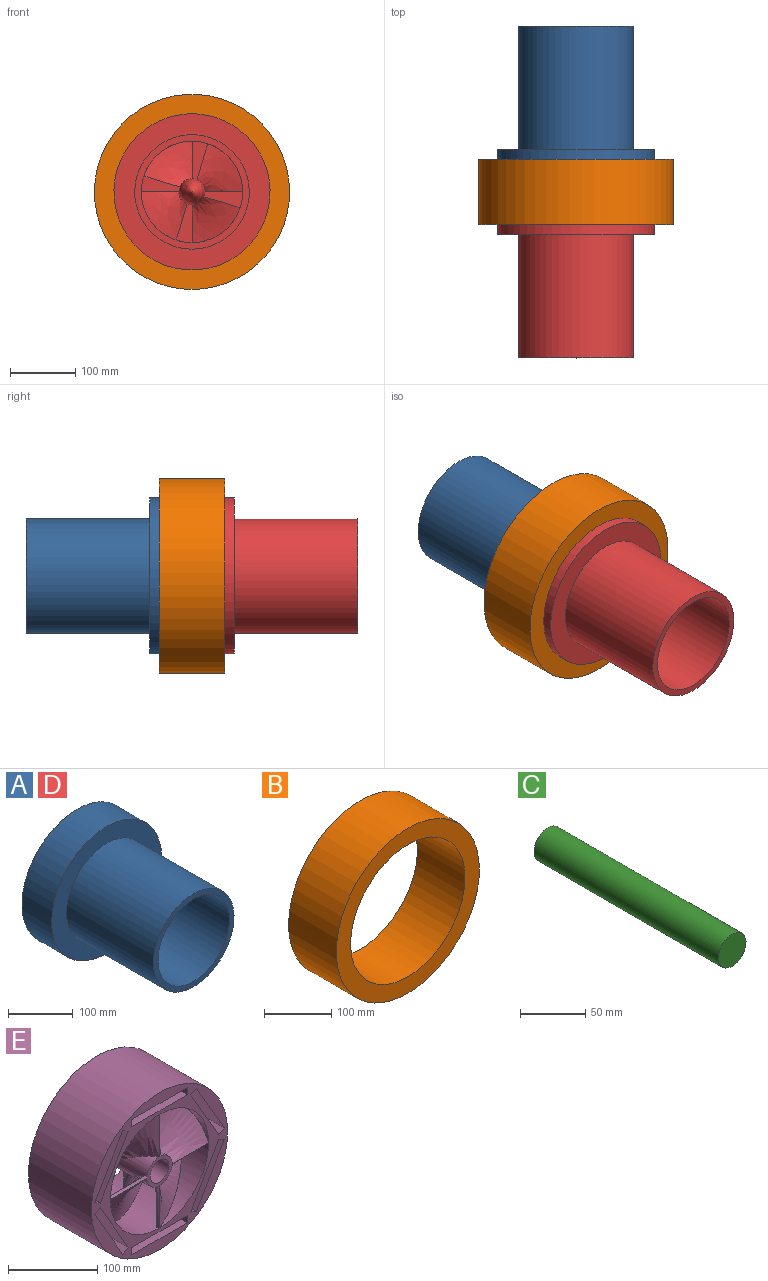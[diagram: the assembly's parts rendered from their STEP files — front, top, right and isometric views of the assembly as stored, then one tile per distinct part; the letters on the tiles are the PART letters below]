
ASSEMBLY  parts=5 mates=4
PART A: 29 faces, bbox 240x255x240 mm
  f0: plane 59.59x24.55mm, normal (0,-1,0), area 943.2mm2, adj f8,f9,f20,f28
  f1: plane 59.59x24.55mm, normal (0,-1,0), area 943.2mm2, adj f11,f12,f20,f28
  f2: plane 59.59x24.55mm, normal (0,-1,0), area 943.2mm2, adj f14,f15,f20,f28
  f3: plane 59.59x24.55mm, normal (0,-1,0), area 943.2mm2, adj f4,f5,f20,f28
  f4: bspline ~48.05x39.74mm, area 17.6mm2, adj f3,f6,f10
  f5: bspline ~156x78mm, area 8501.3mm2, adj f3,f6,f7,f20
  f6: plane 220x220mm, normal (0,1,0), area 23220.2mm2, adj f4,f5,f7,f8,f9,f10,f11,f12
  f7: cylinder r=20mm len=45mm, axis (0,1,0), area 1052.4mm2, adj f5,f6,f14,f28
  f8: bspline ~48.05x39.74mm, area 17.6mm2, adj f0,f6,f13
  f9: bspline ~156x78mm, area 8501.3mm2, adj f0,f6,f10,f20
  f10: cylinder r=20mm len=45mm, axis (0,1,0), area 1052.4mm2, adj f4,f6,f9,f28
  f11: bspline ~48.05x39.74mm, area 17.6mm2, adj f1,f6,f25
  f12: bspline ~156x78mm, area 8501.6mm2, adj f1,f6,f13,f20,f22
  f13: cylinder r=20mm len=45mm, axis (0,1,0), area 1052.4mm2, adj f6,f8,f12,f28
  f14: bspline ~48.05x39.74mm, area 17.6mm2, adj f2,f6,f7
  f15: bspline ~152.19x78mm, area 8501.3mm2, adj f2,f6,f21,f25
  f16: cylinder r=110mm len=220mm, axis (0,1,0), area 38013.3mm2, adj f6,f18
  f17: cylinder r=120mm len=240mm, axis (0,1,0), area 49008.8mm2, adj f18,f19
  f18: plane 240x240mm, normal (0,1,0), area 7225.7mm2, adj f16,f17
  f19: plane 240x240mm, normal (0,-1,0), area 20910.4mm2, adj f17,f23
  f20: cylinder r=78mm len=200mm, axis (0,1,0), area 89123.2mm2, adj f0,f1,f2,f3,f5,f6,f9,f12
  f21: cylinder r=78mm len=152.19mm, axis (0,1,0), area 3419mm2, adj f6,f15,f20
  f22: cylinder r=78mm len=74.19mm, axis (0,1,0), area 974.7mm2, adj f6,f12,f20
  f23: cylinder r=88mm len=190mm, axis (0,1,0), area 105054.9mm2, adj f19,f24
  f24: plane 176x176mm, normal (0,-1,0), area 5215mm2, adj f20,f23
  f25: cylinder r=20mm len=45mm, axis (0,1,0), area 1052.4mm2, adj f6,f11,f15,f28
  f26: cylinder r=15mm len=45mm, axis (0,1,0), area 4241.2mm2, adj f6,f27
  f27: plane 30x30mm, normal (0,1,0), area 706.9mm2, adj f26
  f28: revolved ~45.18x40mm, area 4210.7mm2, adj f0,f1,f2,f3,f7,f10,f13,f25
PART B: 4 faces, bbox 300x100x300 mm
  f0: cylinder r=120mm len=240mm, axis (0,1,0), area 75398.2mm2, adj f2,f3
  f1: cylinder r=150mm len=300mm, axis (0,1,0), area 94247.8mm2, adj f2,f3
  f2: plane 300x300mm, normal (0,-1,0), area 25446.9mm2, adj f0,f1
  f3: plane 300x300mm, normal (0,1,0), area 25446.9mm2, adj f0,f1
PART C: 3 faces, bbox 30x200x30 mm
  f0: cylinder r=15mm len=200mm, axis (0,1,0), area 18849.6mm2, adj f1,f2
  f1: plane 30x30mm, normal (0,-1,0), area 706.9mm2, adj f0
  f2: plane 30x30mm, normal (0,1,0), area 706.9mm2, adj f0
PART D: same geometry as A
PART E: 45 faces, bbox 216x100x216 mm
  f0: cylinder r=78mm len=156mm, axis (0,1,0), area 11212.6mm2, adj f29,f30,f32,f41
  f1: cylinder r=78mm len=156mm, axis (0,1,0), area 11212.6mm2, adj f29,f30,f33,f42
  f2: cylinder r=78mm len=156mm, axis (0,1,0), area 11212.6mm2, adj f29,f30,f34,f43
  f3: plane 100x88.54mm, normal (0,0,1), area 8854.4mm2, adj f4,f28,f29,f30
  f4: plane 100x10mm, normal (1,0,0), area 1000mm2, adj f3,f5,f29,f30
  f5: plane 100x88.54mm, normal (0,0,-1), area 8854.4mm2, adj f4,f28,f29,f30
  f6: plane 100x8.66mm, normal (0.5,0,0.87), area 1000mm2, adj f7,f21,f29,f30
  f7: plane 100x76.68mm, normal (0.87,0,-0.5), area 8854.4mm2, adj f6,f8,f29,f30
  f8: plane 100x8.66mm, normal (-0.5,0,-0.87), area 1000mm2, adj f7,f21,f29,f30
  f9: plane 100x8.66mm, normal (-0.5,0,0.87), area 1000mm2, adj f10,f22,f29,f30
  f10: plane 100x76.68mm, normal (0.87,0,0.5), area 8854.4mm2, adj f9,f11,f29,f30
  f11: plane 100x8.66mm, normal (0.5,0,-0.87), area 1000mm2, adj f10,f22,f29,f30
  f12: plane 100x10mm, normal (-1,0,0), area 1000mm2, adj f13,f23,f29,f30
  f13: plane 100x88.54mm, normal (0,0,1), area 8854.4mm2, adj f12,f14,f29,f30
  f14: plane 100x10mm, normal (1,0,0), area 1000mm2, adj f13,f23,f29,f30
  f15: plane 100x8.66mm, normal (-0.5,0,-0.87), area 1000mm2, adj f16,f24,f29,f30
  f16: plane 100x76.68mm, normal (-0.87,0,0.5), area 8854.4mm2, adj f15,f17,f29,f30
  f17: plane 100x8.66mm, normal (0.5,0,0.87), area 1000mm2, adj f16,f24,f29,f30
  f18: plane 100x8.66mm, normal (0.5,0,-0.87), area 1000mm2, adj f19,f25,f29,f30
  f19: plane 100x76.68mm, normal (-0.87,0,-0.5), area 8854.4mm2, adj f18,f20,f29,f30
  f20: plane 100x8.66mm, normal (-0.5,0,0.87), area 1000mm2, adj f19,f25,f29,f30
  f21: plane 100x76.68mm, normal (-0.87,0,0.5), area 8854.4mm2, adj f6,f8,f29,f30
  f22: plane 100x76.68mm, normal (-0.87,0,-0.5), area 8854.4mm2, adj f9,f11,f29,f30
  f23: plane 100x88.54mm, normal (0,0,-1), area 8854.4mm2, adj f12,f14,f29,f30
  f24: plane 100x76.68mm, normal (0.87,0,-0.5), area 8854.4mm2, adj f15,f17,f29,f30
  f25: plane 100x76.68mm, normal (0.87,0,0.5), area 8854.4mm2, adj f18,f20,f29,f30
  f26: cylinder r=108mm len=216mm, axis (0,1,0), area 67858.4mm2, adj f29,f30
  f27: cylinder r=78mm len=156mm, axis (0,1,0), area 11212.6mm2, adj f29,f30,f31,f44
  f28: plane 100x10mm, normal (-1,0,0), area 1000mm2, adj f3,f5,f29,f30
  f29: plane 216x216mm, normal (0,-1,0), area 12217.5mm2, adj f0,f1,f2,f3,f4,f5,f6,f7
  f30: plane 216x216mm, normal (0,1,0), area 14496.2mm2, adj f0,f1,f2,f3,f4,f5,f6,f7
  f31: bspline ~161.32x100mm, area 10790.1mm2, adj f27,f30,f38,f41
  f32: bspline ~161.32x100mm, area 10790.1mm2, adj f0,f30,f37,f42
  f33: bspline ~161.32x100mm, area 10790.1mm2, adj f1,f30,f36,f43
  f34: bspline ~161.32x100mm, area 10790.1mm2, adj f2,f30,f35,f44
  f35: cylinder r=20mm len=100mm, axis (0,1,0), area 2672.3mm2, adj f30,f34,f40,f43
  f36: cylinder r=20mm len=100mm, axis (0,1,0), area 2672.3mm2, adj f30,f33,f40,f42
  f37: cylinder r=20mm len=100mm, axis (0,1,0), area 2672.3mm2, adj f30,f32,f40,f41
  f38: cylinder r=20mm len=100mm, axis (0,1,0), area 2672.3mm2, adj f30,f31,f40,f44
  f39: cylinder r=15mm len=100mm, axis (0,1,0), area 9424.8mm2, adj f30,f40
  f40: plane 40x40mm, normal (0,-1,0), area 549.8mm2, adj f35,f36,f37,f38,f39
  f41: bspline ~63.6x3.73mm, area 232.6mm2, adj f0,f31,f37
  f42: bspline ~63.6x3.73mm, area 232.6mm2, adj f1,f32,f36
  f43: bspline ~63.6x3.73mm, area 232.6mm2, adj f2,f33,f35
  f44: bspline ~63.6x3.73mm, area 232.6mm2, adj f27,f34,f38
PLACE A rot(axis=(1,0,0),180deg) t=(27.83,10.28,66.33)mm
PLACE B t=(27.83,10.28,66.33)mm
PLACE C rot(axis=(0,-1,0),117.7deg) t=(27.83,10.28,66.33)mm
PLACE D t=(27.83,10.28,66.33)mm fixed
PLACE E rot(axis=(0,-1,0),117.7deg) t=(27.83,10.28,66.33)mm
MATE fastened B.f1 <-> D.f17  axis (0,1,0) through (27.83,10.28,66.33)mm
MATE fastened A.f20 <-> D.f17  axis (0,-1,0) through (27.83,10.28,66.33)mm
MATE fastened C.f0 <-> E.f39  axis (0,1,0) through (27.83,10.28,66.33)mm
MATE revolute C.f0 <-> D.f26  axis (0,-1,0) through (27.83,-89.72,66.33)mm
